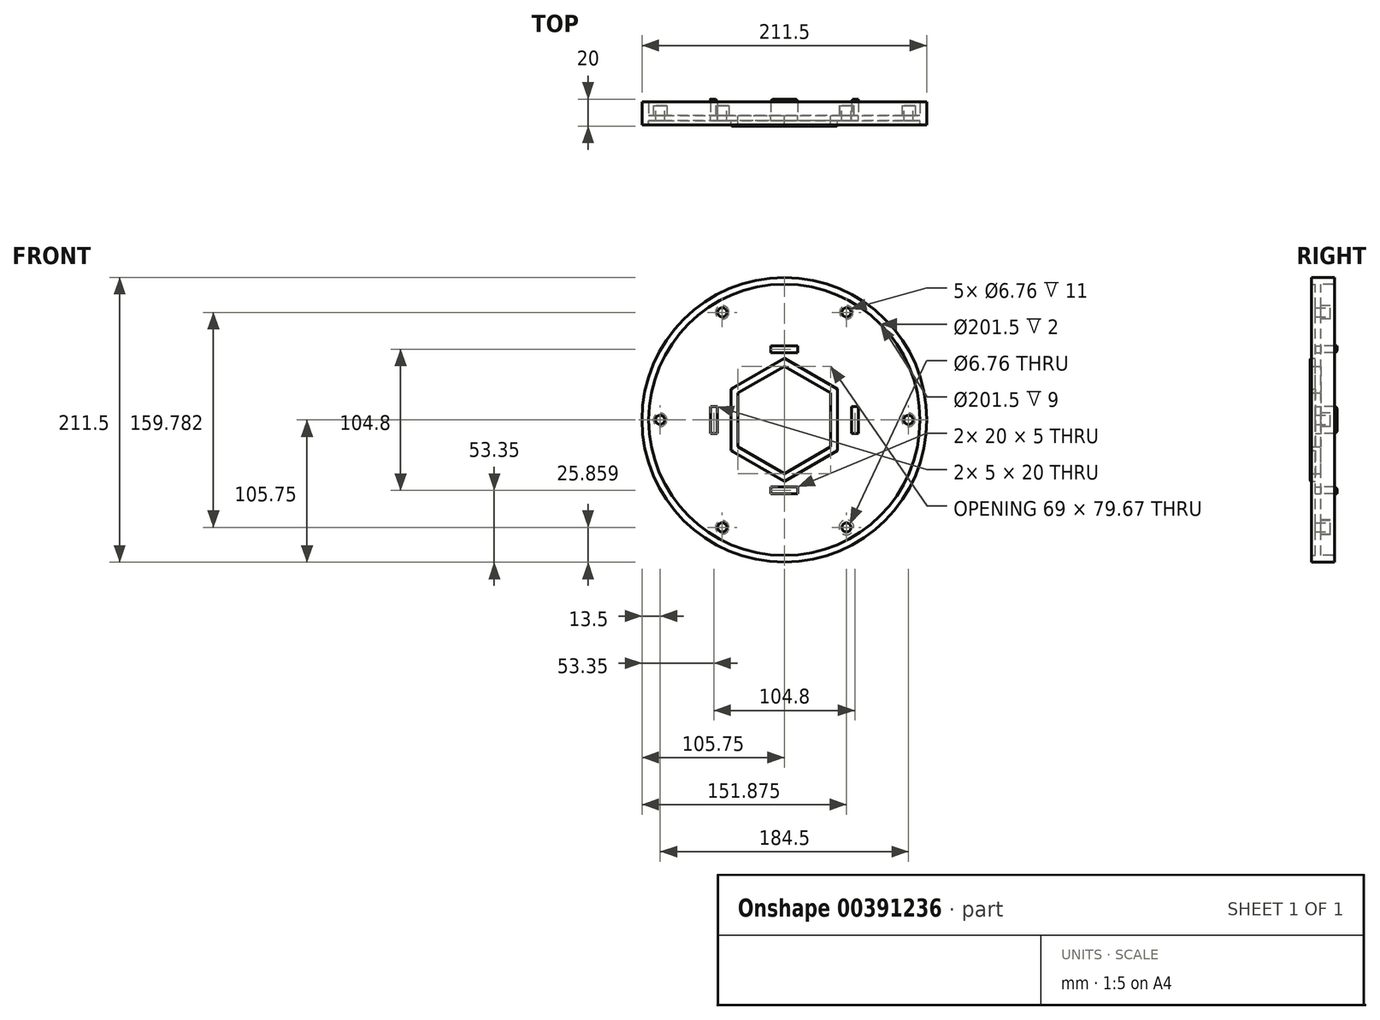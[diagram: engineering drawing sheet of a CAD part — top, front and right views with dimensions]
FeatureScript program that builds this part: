
annotation { "Feature Type Name" : "Feature", "Feature Type Description" : "" }
export const myFeature = defineFeature(function(context is Context, id is Id, definition is map)
    precondition{}
    {
        {
            var Q0;
            Q0=qCreatedBy(makeId("Front.planeOp"),FACE);
            var sketch = newSketch(context, id + "F0", { "sketchPlane" : qUnion([Q0])});
            skCircle(sketch, "E0.cCircle", {"center": v(0, 0) * mm, "radius": 80.5 * mm, "construction": true});
            skLineSegment(sketch, "E0.0", {"start": v(80.5, -46.48) * mm, "end": v(0, -92.95) * mm});
            skLineSegment(sketch, "E0.1", {"start": v(0, -92.95) * mm, "end": v(-80.5, -46.48) * mm});
            skLineSegment(sketch, "E0.2", {"start": v(-80.5, -46.48) * mm, "end": v(-80.5, 46.48) * mm});
            skLineSegment(sketch, "E0.3", {"start": v(-80.5, 46.48) * mm, "end": v(0, 92.95) * mm});
            skLineSegment(sketch, "E0.4", {"start": v(0, 92.95) * mm, "end": v(80.5, 46.48) * mm});
            skLineSegment(sketch, "E0.5", {"start": v(80.5, 46.48) * mm, "end": v(80.5, -46.48) * mm});
            skPoint(sketch, "E0.0.midPoint", {"position": v(40.25, -69.72) * mm});
            skPoint(sketch, "E1.0.midPoint", {"position": v(83.75, 0) * mm});
            skCircle(sketch, "E2", {"center": v(0, 0) * mm, "radius": 100.75 * mm});
            skPoint(sketch, "E3.0.midPoint", {"position": v(19.75, -35.93) * mm});
            skCircle(sketch, "E4.cCircle", {"center": v(0, 0) * mm, "radius": 34.5 * mm, "construction": true});
            skLineSegment(sketch, "E4.0", {"start": v(34.5, -19.92) * mm, "end": v(0, -39.84) * mm});
            skLineSegment(sketch, "E4.1", {"start": v(0, -39.84) * mm, "end": v(-34.5, -19.92) * mm});
            skLineSegment(sketch, "E4.2", {"start": v(-34.5, -19.92) * mm, "end": v(-34.5, 19.92) * mm});
            skLineSegment(sketch, "E4.3", {"start": v(-34.5, 19.92) * mm, "end": v(0, 39.84) * mm});
            skLineSegment(sketch, "E4.4", {"start": v(0, 39.84) * mm, "end": v(34.5, 19.92) * mm});
            skLineSegment(sketch, "E4.5", {"start": v(34.5, 19.92) * mm, "end": v(34.5, -19.92) * mm});
            skPoint(sketch, "E4.0.midPoint", {"position": v(17.25, -29.88) * mm});
            skPoint(sketch, "E5.visualSharp", {"position": v(0, 96.7) * mm});
            skPoint(sketch, "E6.visualSharp", {"position": v(83.75, 48.35) * mm});
            skPoint(sketch, "E7.visualSharp", {"position": v(83.75, -48.35) * mm});
            skPoint(sketch, "E8.visualSharp", {"position": v(0, -96.7) * mm});
            skPoint(sketch, "E9.visualSharp", {"position": v(-83.75, -48.35) * mm});
            skPoint(sketch, "E10.visualSharp", {"position": v(-83.75, 48.35) * mm});
            skPoint(sketch, "E11.visualSharp", {"position": v(39.66, 22.9) * mm});
            skPoint(sketch, "E12.visualSharp", {"position": v(39.58, -24.48) * mm});
            skPoint(sketch, "E13.visualSharp", {"position": v(-0.08, -47.38) * mm});
            skPoint(sketch, "E14.visualSharp", {"position": v(-39.66, -22.9) * mm});
            skPoint(sketch, "E15.visualSharp", {"position": v(-39.66, 22.9) * mm});
            skPoint(sketch, "E16.visualSharp", {"position": v(0, 45.8) * mm});
            skCircle(sketch, "E17.cCircle", {"center": v(0, 0) * mm, "radius": 77.5 * mm, "construction": true});
            skLineSegment(sketch, "E17.0", {"start": v(77.5, 44.74) * mm, "end": v(77.5, -44.74) * mm});
            skLineSegment(sketch, "E17.1", {"start": v(77.5, -44.74) * mm, "end": v(0, -89.49) * mm});
            skLineSegment(sketch, "E17.2", {"start": v(0, -89.49) * mm, "end": v(-77.5, -44.74) * mm});
            skLineSegment(sketch, "E17.3", {"start": v(-77.5, -44.74) * mm, "end": v(-77.5, 44.74) * mm});
            skLineSegment(sketch, "E17.4", {"start": v(-77.5, 44.74) * mm, "end": v(0, 89.49) * mm});
            skLineSegment(sketch, "E17.5", {"start": v(0, 89.49) * mm, "end": v(77.5, 44.74) * mm});
            skPoint(sketch, "E17.0.midPoint", {"position": v(77.5, 0) * mm});
            skCircle(sketch, "E18.cCircle", {"center": v(0, 0) * mm, "radius": 39.5 * mm, "construction": true});
            skLineSegment(sketch, "E18.0", {"start": v(39.5, -22.8) * mm, "end": v(0, -45.61) * mm});
            skLineSegment(sketch, "E18.1", {"start": v(0, -45.61) * mm, "end": v(-39.5, -22.8) * mm});
            skLineSegment(sketch, "E18.2", {"start": v(-39.5, -22.8) * mm, "end": v(-39.5, 22.8) * mm});
            skLineSegment(sketch, "E18.3", {"start": v(-39.5, 22.8) * mm, "end": v(0, 45.61) * mm});
            skLineSegment(sketch, "E18.4", {"start": v(0, 45.61) * mm, "end": v(39.5, 22.8) * mm});
            skLineSegment(sketch, "E18.5", {"start": v(39.5, 22.8) * mm, "end": v(39.5, -22.8) * mm});
            skPoint(sketch, "E18.0.midPoint", {"position": v(19.75, -34.2) * mm});
            skCircle(sketch, "E19", {"center": v(0, 0) * mm, "radius": 105.75 * mm});
            skPoint(sketch, "E20", {"position": v(-46.12, 79.9) * mm});
            skPoint(sketch, "E21", {"position": v(46.12, 79.9) * mm});
            skPoint(sketch, "E22", {"position": v(92.25, 0) * mm});
            skPoint(sketch, "E23", {"position": v(46.13, -79.9) * mm});
            skPoint(sketch, "E24", {"position": v(-46.12, -79.9) * mm});
            skPoint(sketch, "E25", {"position": v(-92.25, 0) * mm});
            skCircle(sketch, "E26.cCircle", {"center": v(0, 0) * mm, "radius": 49.9 * mm, "construction": true});
            skLineSegment(sketch, "E26.0", {"start": v(49.9, -49.9) * mm, "end": v(-49.9, -49.9) * mm});
            skLineSegment(sketch, "E26.1", {"start": v(-49.9, -49.9) * mm, "end": v(-49.9, 49.9) * mm});
            skLineSegment(sketch, "E26.2", {"start": v(-49.9, 49.9) * mm, "end": v(49.9, 49.9) * mm});
            skLineSegment(sketch, "E26.3", {"start": v(49.9, 49.9) * mm, "end": v(49.9, -49.9) * mm});
            skPoint(sketch, "E26.0.midPoint", {"position": v(0, -49.9) * mm});
            skCircle(sketch, "E27", {"center": v(46.12, 79.9) * mm, "radius": 5 * mm});
            skCircle(sketch, "E28", {"center": v(92.25, 0) * mm, "radius": 5 * mm});
            skCircle(sketch, "E29", {"center": v(46.13, -79.9) * mm, "radius": 5.54 * mm});
            skCircle(sketch, "E30", {"center": v(-46.12, -79.9) * mm, "radius": 5 * mm});
            skCircle(sketch, "E31", {"center": v(-92.25, 0) * mm, "radius": 5 * mm});
            skCircle(sketch, "E32", {"center": v(-46.12, 79.9) * mm, "radius": 5 * mm});
            skPoint(sketch, "E33", {"position": v(10, -49.9) * mm});
            skPoint(sketch, "E34", {"position": v(-10, -49.9) * mm});
            skPoint(sketch, "E35", {"position": v(-10, -54.9) * mm});
            skPoint(sketch, "E36", {"position": v(10, -54.9) * mm});
            skLineSegment(sketch, "E37", {"start": v(-10, -49.9) * mm, "end": v(-10, -54.9) * mm});
            skLineSegment(sketch, "E38", {"start": v(-10, -54.9) * mm, "end": v(10, -54.9) * mm});
            skLineSegment(sketch, "E39", {"start": v(10, -54.9) * mm, "end": v(10, -49.9) * mm});
            skPoint(sketch, "E40", {"position": v(49.9, 0) * mm});
            skPoint(sketch, "E41", {"position": v(0, 49.9) * mm});
            skPoint(sketch, "E42", {"position": v(-49.9, 0) * mm});
            skPoint(sketch, "E43", {"position": v(49.9, -10) * mm});
            skPoint(sketch, "E44", {"position": v(49.9, 10) * mm});
            skPoint(sketch, "E45", {"position": v(54.9, -10) * mm});
            skPoint(sketch, "E46", {"position": v(54.9, 10) * mm});
            skLineSegment(sketch, "E47", {"start": v(49.9, -10) * mm, "end": v(54.9, -10) * mm});
            skLineSegment(sketch, "E48", {"start": v(54.9, 10) * mm, "end": v(54.9, -10) * mm});
            skLineSegment(sketch, "E49", {"start": v(49.9, 10) * mm, "end": v(54.9, 10) * mm});
            skPoint(sketch, "E50", {"position": v(10, 49.9) * mm});
            skPoint(sketch, "E51", {"position": v(10, 54.9) * mm});
            skPoint(sketch, "E52", {"position": v(-10, 49.9) * mm});
            skPoint(sketch, "E53", {"position": v(-10, 54.9) * mm});
            skLineSegment(sketch, "E54", {"start": v(10, 49.9) * mm, "end": v(10, 54.9) * mm});
            skLineSegment(sketch, "E55", {"start": v(10, 54.9) * mm, "end": v(-10, 54.9) * mm});
            skLineSegment(sketch, "E56", {"start": v(-10, 54.9) * mm, "end": v(-10, 49.9) * mm});
            skPoint(sketch, "E57", {"position": v(-49.9, -10) * mm});
            skPoint(sketch, "E58", {"position": v(-54.9, -10) * mm});
            skPoint(sketch, "E59", {"position": v(-49.9, 10) * mm});
            skPoint(sketch, "E60", {"position": v(-54.9, 10) * mm});
            skLineSegment(sketch, "E61", {"start": v(-49.9, -10) * mm, "end": v(-54.9, -10) * mm});
            skLineSegment(sketch, "E62", {"start": v(-54.9, -10) * mm, "end": v(-54.9, 10) * mm});
            skLineSegment(sketch, "E63", {"start": v(-54.9, 10) * mm, "end": v(-49.9, 10) * mm});
            skSolve(sketch);
        }
        {
            var Q0;
            Q0=makeQuery(id+"F0.imprint","IMPRINT",FACE,{"disambiguationData":[TD([[makeQuery(id+"F0.imprint","IMPRINT",EDGE,{"derivedFrom":sQuery(id+"F0.wireOp",EDGE,"E0.0")}),1.0]])]});
            var Q1;
            Q1=makeQuery(id+"F0.imprint","IMPRINT",FACE,{"disambiguationData":[TD([[makeQuery(id+"F0.imprint","IMPRINT",EDGE,{"derivedFrom":sQuery(id+"F0.wireOp",EDGE,"E17.0")}),-1.0]])]});
            var Q2;
            {var subQ0=sQuery(id+"F0.wireOp",EDGE,"E26.1");var subQ1=sQuery(id+"F0.wireOp",EDGE,"E18.3");var subQ2=makeQuery(id+"F0.imprint","INTERSECT",VERTEX,{"derivedFrom":[subQ1,subQ0]});Q2=makeQuery(id+"F0.imprint","IMPRINT",FACE,{"disambiguationData":[TD([[makeQuery(id+"F0.imprint","IMPRINT",EDGE,{"disambiguationData":[TD([[subQ2,-1.0]])],"derivedFrom":subQ1}),1.0]])]});}
            var Q3;
            {var subQ0=sQuery(id+"F0.wireOp",EDGE,"E26.2");var subQ1=sQuery(id+"F0.wireOp",EDGE,"E18.4");var subQ2=makeQuery(id+"F0.imprint","INTERSECT",VERTEX,{"derivedFrom":[subQ1,subQ0]});Q3=makeQuery(id+"F0.imprint","IMPRINT",FACE,{"disambiguationData":[TD([[makeQuery(id+"F0.imprint","IMPRINT",EDGE,{"disambiguationData":[TD([[subQ2,-1.0]])],"derivedFrom":subQ1}),1.0]])]});}
            var Q4;
            {var subQ0=sQuery(id+"F0.wireOp",EDGE,"E26.0");var subQ1=sQuery(id+"F0.wireOp",EDGE,"E18.1");var subQ2=makeQuery(id+"F0.imprint","INTERSECT",VERTEX,{"derivedFrom":[subQ1,subQ0]});Q4=makeQuery(id+"F0.imprint","IMPRINT",FACE,{"disambiguationData":[TD([[makeQuery(id+"F0.imprint","IMPRINT",EDGE,{"disambiguationData":[TD([[subQ2,-1.0]])],"derivedFrom":subQ1}),1.0]])]});}
            var Q5;
            {var subQ0=sQuery(id+"F0.wireOp",EDGE,"E26.3");var subQ1=sQuery(id+"F0.wireOp",EDGE,"E18.0");var subQ2=makeQuery(id+"F0.imprint","INTERSECT",VERTEX,{"derivedFrom":[subQ1,subQ0]});Q5=makeQuery(id+"F0.imprint","IMPRINT",FACE,{"disambiguationData":[TD([[makeQuery(id+"F0.imprint","IMPRINT",EDGE,{"disambiguationData":[TD([[subQ2,-1.0]])],"derivedFrom":subQ1}),1.0]])]});}
            var Q6;
            {var subQ0=sQuery(id+"F0.wireOp",EDGE,"XCPQ21YX-vmVf-RJUl-SYTq-fUJmevbIAi7m");var subQ1=sQuery(id+"F0.wireOp",EDGE,"E18.0");var subQ2=makeQuery(id+"F0.imprint","INTERSECT",VERTEX,{"derivedFrom":[subQ1,subQ0]});Q6=makeQuery(id+"F0.imprint","IMPRINT",FACE,{"disambiguationData":[TD([[makeQuery(id+"F0.imprint","IMPRINT",EDGE,{"disambiguationData":[TD([[subQ2,-1.0]])],"derivedFrom":subQ1}),1.0]])]});}
            var Q7;
            Q7=makeQuery(id+"F0.imprint","IMPRINT",FACE,{"disambiguationData":[TD([[makeQuery(id+"F0.imprint","IMPRINT",EDGE,{"derivedFrom":sQuery(id+"F0.wireOp",EDGE,"E32")}),1.0]])]});
            var Q8;
            Q8=makeQuery(id+"F0.imprint","IMPRINT",FACE,{"disambiguationData":[TD([[makeQuery(id+"F0.imprint","IMPRINT",EDGE,{"derivedFrom":sQuery(id+"F0.wireOp",EDGE,"E27")}),1.0]])]});
            var Q9;
            Q9=makeQuery(id+"F0.imprint","IMPRINT",FACE,{"disambiguationData":[TD([[makeQuery(id+"F0.imprint","IMPRINT",EDGE,{"derivedFrom":sQuery(id+"F0.wireOp",EDGE,"E28")}),1.0]])]});
            var Q10;
            Q10=makeQuery(id+"F0.imprint","IMPRINT",FACE,{"disambiguationData":[TD([[makeQuery(id+"F0.imprint","IMPRINT",EDGE,{"derivedFrom":sQuery(id+"F0.wireOp",EDGE,"E29")}),1.0]])]});
            var Q11;
            Q11=makeQuery(id+"F0.imprint","IMPRINT",FACE,{"disambiguationData":[TD([[makeQuery(id+"F0.imprint","IMPRINT",EDGE,{"derivedFrom":sQuery(id+"F0.wireOp",EDGE,"E30")}),1.0]])]});
            var Q12;
            Q12=makeQuery(id+"F0.imprint","IMPRINT",FACE,{"disambiguationData":[TD([[makeQuery(id+"F0.imprint","IMPRINT",EDGE,{"derivedFrom":sQuery(id+"F0.wireOp",EDGE,"E31")}),1.0]])]});
            extrude(context, id + "F1", {"entities" : qUnion([Q0, Q1, Q2, Q3, Q4, Q5, Q6, Q7, Q8, Q9, Q10, Q11, Q12]), "depth" : 4 * mm});
        }
        {
            var Q0;
            Q0=makeQuery(id+"F0.imprint","IMPRINT",FACE,{"disambiguationData":[TD([[makeQuery(id+"F0.imprint","IMPRINT",EDGE,{"derivedFrom":sQuery(id+"F0.wireOp",EDGE,"E0.0")}),-1.0]])]});
            extrude(context, id + "F2", {"entities" : qUnion([Q0]), "depth" : 4 * mm});
        }
        {
            var Q0;
            Q0=makeQuery(id+"F0.imprint","IMPRINT",FACE,{"disambiguationData":[TD([[makeQuery(id+"F0.imprint","IMPRINT",EDGE,{"derivedFrom":sQuery(id+"F0.wireOp",EDGE,"E4.0")}),1.0]])]});
            var Q1;
            {var subQ5=sQuery(id+"F0.wireOp",EDGE,"E4.1");var subQ6=sQuery(id+"F0.wireOp",EDGE,"E4.0");var subQ7=makeQuery(id+"F0.imprint","INTERSECT",VERTEX,{"derivedFrom":[subQ6,subQ5]});Q1=makeQuery(id+"F0.imprint","IMPRINT",FACE,{"disambiguationData":[TD([[makeQuery(id+"F0.imprint","IMPRINT",EDGE,{"disambiguationData":[TD([[subQ7,1.0]])],"derivedFrom":subQ6}),1.0]])]});}
            var Q2;
            {var subQ0=sQuery(id+"F0.wireOp",EDGE,"E26.0");var subQ1=sQuery(id+"F0.wireOp",EDGE,"E4.1");var subQ2=makeQuery(id+"F0.imprint","INTERSECT",VERTEX,{"derivedFrom":[subQ1,subQ0]});Q2=makeQuery(id+"F0.imprint","IMPRINT",FACE,{"disambiguationData":[TD([[makeQuery(id+"F0.imprint","IMPRINT",EDGE,{"disambiguationData":[TD([[subQ2,-1.0]])],"derivedFrom":subQ1}),1.0]])]});}
            var Q3;
            {var subQ1=sQuery(id+"F0.wireOp",EDGE,"E4.2");Q3=makeQuery(id+"F0.imprint","IMPRINT",FACE,{"disambiguationData":[TD([[makeQuery(id+"F0.imprint","IMPRINT",EDGE,{"derivedFrom":subQ1}),1.0]])]});}
            var Q4;
            {var subQ0=sQuery(id+"F0.wireOp",EDGE,"E26.1");var subQ1=sQuery(id+"F0.wireOp",EDGE,"E4.3");var subQ2=makeQuery(id+"F0.imprint","INTERSECT",VERTEX,{"derivedFrom":[subQ1,subQ0]});Q4=makeQuery(id+"F0.imprint","IMPRINT",FACE,{"disambiguationData":[TD([[makeQuery(id+"F0.imprint","IMPRINT",EDGE,{"disambiguationData":[TD([[subQ2,-1.0]])],"derivedFrom":subQ1}),1.0]])]});}
            var Q5;
            {var subQ5=sQuery(id+"F0.wireOp",EDGE,"E4.4");var subQ6=sQuery(id+"F0.wireOp",EDGE,"E4.3");var subQ7=makeQuery(id+"F0.imprint","INTERSECT",VERTEX,{"derivedFrom":[subQ6,subQ5]});Q5=makeQuery(id+"F0.imprint","IMPRINT",FACE,{"disambiguationData":[TD([[makeQuery(id+"F0.imprint","IMPRINT",EDGE,{"disambiguationData":[TD([[subQ7,1.0]])],"derivedFrom":subQ6}),1.0]])]});}
            var Q6;
            {var subQ0=sQuery(id+"F0.wireOp",EDGE,"E26.2");var subQ1=sQuery(id+"F0.wireOp",EDGE,"E4.4");var subQ2=makeQuery(id+"F0.imprint","INTERSECT",VERTEX,{"derivedFrom":[subQ1,subQ0]});Q6=makeQuery(id+"F0.imprint","IMPRINT",FACE,{"disambiguationData":[TD([[makeQuery(id+"F0.imprint","IMPRINT",EDGE,{"disambiguationData":[TD([[subQ2,-1.0]])],"derivedFrom":subQ1}),1.0]])]});}
            var Q7;
            {var subQ0=sQuery(id+"F0.wireOp",EDGE,"E4.5");Q7=makeQuery(id+"F0.imprint","IMPRINT",FACE,{"disambiguationData":[TD([[makeQuery(id+"F0.imprint","IMPRINT",EDGE,{"derivedFrom":subQ0}),1.0]])]});}
            var Q8;
            {var subQ0=sQuery(id+"F0.wireOp",EDGE,"XCPQ21YX-vmVf-RJUl-SYTq-fUJmevbIAi7m");var subQ1=sQuery(id+"F0.wireOp",EDGE,"E4.0");var subQ2=makeQuery(id+"F0.imprint","INTERSECT",VERTEX,{"derivedFrom":[subQ1,subQ0]});Q8=makeQuery(id+"F0.imprint","IMPRINT",FACE,{"disambiguationData":[TD([[makeQuery(id+"F0.imprint","IMPRINT",EDGE,{"disambiguationData":[TD([[subQ2,-1.0]])],"derivedFrom":subQ1}),1.0]])]});}
            var Q9;
            {var subQ1=sQuery(id+"F0.wireOp",EDGE,"E4.0");var subQ5=sQuery(id+"F0.wireOp",EDGE,"nueKWM4Y-l1hd-9WO2-oQTT-vtyMg7v0kKZ8");var subQ9=makeQuery(id+"F0.imprint","INTERSECT",VERTEX,{"derivedFrom":[subQ1,subQ5]});Q9=makeQuery(id+"F0.imprint","IMPRINT",FACE,{"disambiguationData":[TD([[makeQuery(id+"F0.imprint","IMPRINT",EDGE,{"disambiguationData":[TD([[subQ9,-1.0]])],"derivedFrom":subQ1}),1.0]])]});}
            extrude(context, id + "F3", {"entities" : qUnion([Q0, Q1, Q2, Q3, Q4, Q5, Q6, Q7, Q8, Q9]), "operationType" : NewBodyOperationType.ADD, "depth" : 8 * mm});
        }
        {
            var Q0;
            Q0=makeQuery(id+"F0.imprint","IMPRINT",FACE,{"disambiguationData":[TD([[makeQuery(id+"F0.imprint","IMPRINT",EDGE,{"derivedFrom":sQuery(id+"F0.wireOp",EDGE,"E2")}),-1.0]])]});
            extrude(context, id + "F4", {"entities" : qUnion([Q0]), "operationType" : NewBodyOperationType.ADD, "depth" : 7 * mm});
        }
        {
            var Q0;
            Q0=makeQuery(id+"F1.opExtrude","SWEPT_BODY",BODY,{"disambiguationData":[OSD([sQuery(id+"F0.wireOp",EDGE,"E0.0"),sQuery(id+"F0.wireOp",EDGE,"E0.1"),sQuery(id+"F0.wireOp",EDGE,"E0.2"),sQuery(id+"F0.wireOp",EDGE,"E0.3"),sQuery(id+"F0.wireOp",EDGE,"E0.4"),sQuery(id+"F0.wireOp",EDGE,"E0.5"),sQuery(id+"F0.wireOp",EDGE,"E2")])]});
            var Q1;
            Q1=makeQuery(id+"F1.opExtrude","SWEPT_BODY",BODY,{"disambiguationData":[OSD([sQuery(id+"F0.wireOp",EDGE,"E17.0"),sQuery(id+"F0.wireOp",EDGE,"E17.1"),sQuery(id+"F0.wireOp",EDGE,"E17.2"),sQuery(id+"F0.wireOp",EDGE,"E17.3"),sQuery(id+"F0.wireOp",EDGE,"E17.4"),sQuery(id+"F0.wireOp",EDGE,"E17.5"),sQuery(id+"F0.wireOp",EDGE,"E18.0"),sQuery(id+"F0.wireOp",EDGE,"E18.1"),sQuery(id+"F0.wireOp",EDGE,"E18.2"),sQuery(id+"F0.wireOp",EDGE,"E18.3"),sQuery(id+"F0.wireOp",EDGE,"E18.4"),sQuery(id+"F0.wireOp",EDGE,"E18.5")])]});
            var Q2;
            Q2=makeQuery(id+"F2.opExtrude","SWEPT_BODY",BODY,{"disambiguationData":[OSD([sQuery(id+"F0.wireOp",EDGE,"E0.0"),sQuery(id+"F0.wireOp",EDGE,"E0.1"),sQuery(id+"F0.wireOp",EDGE,"E0.2"),sQuery(id+"F0.wireOp",EDGE,"E0.3"),sQuery(id+"F0.wireOp",EDGE,"E0.4"),sQuery(id+"F0.wireOp",EDGE,"E0.5"),sQuery(id+"F0.wireOp",EDGE,"E17.0"),sQuery(id+"F0.wireOp",EDGE,"E17.1"),sQuery(id+"F0.wireOp",EDGE,"E17.2"),sQuery(id+"F0.wireOp",EDGE,"E17.3"),sQuery(id+"F0.wireOp",EDGE,"E17.4"),sQuery(id+"F0.wireOp",EDGE,"E17.5")])]});
            booleanBodies(context, id + "F5", {"operationType" : BooleanOperationType.UNION, "tools" : qUnion([Q0, Q1, Q2])});
        }
        {
            var Q0;
            Q0=makeQuery(id+"F3.opExtrude","CAP_EDGE",EDGE,{"disambiguationData":[OSD([sQuery(id+"F0.wireOp",EDGE,"E18.4")])],"isStart":false});
            var Q1;
            Q1=makeQuery(id+"F3.opExtrude","CAP_EDGE",EDGE,{"disambiguationData":[OSD([sQuery(id+"F0.wireOp",EDGE,"E18.5")])],"isStart":false});
            var Q2;
            Q2=makeQuery(id+"F3.opExtrude","CAP_EDGE",EDGE,{"disambiguationData":[OSD([sQuery(id+"F0.wireOp",EDGE,"E18.0")])],"isStart":false});
            var Q3;
            Q3=makeQuery(id+"F3.opExtrude","CAP_EDGE",EDGE,{"disambiguationData":[OSD([sQuery(id+"F0.wireOp",EDGE,"E18.1")])],"isStart":false});
            var Q4;
            Q4=makeQuery(id+"F3.opExtrude","CAP_EDGE",EDGE,{"disambiguationData":[OSD([sQuery(id+"F0.wireOp",EDGE,"E18.2")])],"isStart":false});
            var Q5;
            Q5=makeQuery(id+"F3.opExtrude","CAP_EDGE",EDGE,{"disambiguationData":[OSD([sQuery(id+"F0.wireOp",EDGE,"E18.3")])],"isStart":false});
            fillet(context, id + "F6", {"entities" : qUnion([Q0, Q1, Q2, Q3, Q4, Q5]), "radius" : 1 * mm, "tangentPropagation" : true, "allowEdgeOverflow" : false});
        }
        {
            var Q0;
            Q0=sQuery(id+"F0.wireOp",VERTEX,"E20");
            var Q1;
            Q1=sQuery(id+"F0.wireOp",VERTEX,"E21");
            var Q2;
            Q2=sQuery(id+"F0.wireOp",VERTEX,"E22");
            var Q3;
            Q3=sQuery(id+"F0.wireOp",VERTEX,"E23");
            var Q4;
            Q4=sQuery(id+"F0.wireOp",VERTEX,"E24");
            var Q5;
            Q5=sQuery(id+"F0.wireOp",VERTEX,"E25");
            var Q6;
            Q6=makeQuery(id+"F1.opExtrude","SWEPT_BODY",BODY,{"disambiguationData":[OSD([sQuery(id+"F0.wireOp",EDGE,"E0.0"),sQuery(id+"F0.wireOp",EDGE,"E0.1"),sQuery(id+"F0.wireOp",EDGE,"E0.2"),sQuery(id+"F0.wireOp",EDGE,"E0.3"),sQuery(id+"F0.wireOp",EDGE,"E0.4"),sQuery(id+"F0.wireOp",EDGE,"E0.5"),sQuery(id+"F0.wireOp",EDGE,"E2")])]});
            hole(context, id + "F7", {"style" : HoleStyle.SIMPLE, "endStyle" : HoleEndStyle.THROUGH, "oppositeDirection" : true, "standardTappedOrClearance" : lookupTablePath({ "standard" : "ANSI", "fit" : "Normal (ASME)", "size" : "1/4", "type" : "Clearance" }), "standardBlindInLast" : lookupTablePath({ "fit" : "Free", "standard" : "ANSI", "size" : "1/4", "type" : "Clearance" }), "holeDiameter" : 6.76 * mm, "tappedDepth" : 12 * mm, "tapClearance" : 3, "locations" : qUnion([Q0, Q1, Q2, Q3, Q4, Q5]), "scope" : qUnion([Q6])});
        }
        {
            var Q0;
            Q0=makeQuery(id+"F4.opExtrude","CAP_EDGE",EDGE,{"disambiguationData":[OSD([sQuery(id+"F0.wireOp",EDGE,"E2")])],"isStart":false});
            fillet(context, id + "F8", {"entities" : qUnion([Q0]), "radius" : 1 * mm, "tangentPropagation" : true, "allowEdgeOverflow" : false});
        }
        {
            var Q0;
            Q0=makeQuery(id+"F0.imprint","IMPRINT",FACE,{"disambiguationData":[TD([[makeQuery(id+"F0.imprint","IMPRINT",EDGE,{"derivedFrom":sQuery(id+"F0.wireOp",EDGE,"E32")}),1.0]])]});
            var Q1;
            Q1=makeQuery(id+"F0.imprint","IMPRINT",FACE,{"disambiguationData":[TD([[makeQuery(id+"F0.imprint","IMPRINT",EDGE,{"derivedFrom":sQuery(id+"F0.wireOp",EDGE,"E27")}),1.0]])]});
            var Q2;
            Q2=makeQuery(id+"F0.imprint","IMPRINT",FACE,{"disambiguationData":[TD([[makeQuery(id+"F0.imprint","IMPRINT",EDGE,{"derivedFrom":sQuery(id+"F0.wireOp",EDGE,"E28")}),1.0]])]});
            var Q3;
            Q3=makeQuery(id+"F0.imprint","IMPRINT",FACE,{"disambiguationData":[TD([[makeQuery(id+"F0.imprint","IMPRINT",EDGE,{"derivedFrom":sQuery(id+"F0.wireOp",EDGE,"E29")}),1.0]])]});
            var Q4;
            Q4=makeQuery(id+"F0.imprint","IMPRINT",FACE,{"disambiguationData":[TD([[makeQuery(id+"F0.imprint","IMPRINT",EDGE,{"derivedFrom":sQuery(id+"F0.wireOp",EDGE,"E30")}),1.0]])]});
            var Q5;
            Q5=makeQuery(id+"F0.imprint","IMPRINT",FACE,{"disambiguationData":[TD([[makeQuery(id+"F0.imprint","IMPRINT",EDGE,{"derivedFrom":sQuery(id+"F0.wireOp",EDGE,"E31")}),1.0]])]});
            extrude(context, id + "F9", {"entities" : qUnion([Q0, Q1, Q2, Q3, Q4, Q5]), "operationType" : NewBodyOperationType.ADD, "oppositeDirection" : true, "depth" : 7 * mm});
        }
        {
            var Q0;
            Q0=makeQuery(id+"F0.imprint","IMPRINT",FACE,{"disambiguationData":[TD([[makeQuery(id+"F0.imprint","IMPRINT",EDGE,{"derivedFrom":sQuery(id+"F0.wireOp",EDGE,"E2")}),-1.0]])]});
            extrude(context, id + "F10", {"entities" : qUnion([Q0]), "operationType" : NewBodyOperationType.ADD, "oppositeDirection" : true, "depth" : 10 * mm});
        }
        {
            var Q0;
            Q0=sQuery(id+"F0.wireOp",VERTEX,"E32.center");
            var Q1;
            Q1=sQuery(id+"F0.wireOp",VERTEX,"E27.center");
            var Q2;
            Q2=sQuery(id+"F0.wireOp",VERTEX,"E22");
            var Q3;
            Q3=sQuery(id+"F0.wireOp",VERTEX,"E23");
            var Q4;
            Q4=sQuery(id+"F0.wireOp",VERTEX,"E24");
            var Q5;
            Q5=sQuery(id+"F0.wireOp",VERTEX,"E25");
            var Q6;
            Q6=makeQuery(id+"F1.opExtrude","SWEPT_BODY",BODY,{"disambiguationData":[OSD([sQuery(id+"F0.wireOp",EDGE,"E0.0"),sQuery(id+"F0.wireOp",EDGE,"E0.1"),sQuery(id+"F0.wireOp",EDGE,"E0.2"),sQuery(id+"F0.wireOp",EDGE,"E0.3"),sQuery(id+"F0.wireOp",EDGE,"E0.4"),sQuery(id+"F0.wireOp",EDGE,"E0.5"),sQuery(id+"F0.wireOp",EDGE,"E2")])]});
            hole(context, id + "F11", {"style" : HoleStyle.SIMPLE, "endStyle" : HoleEndStyle.THROUGH, "standardTappedOrClearance" : lookupTablePath({ "standard" : "ANSI", "fit" : "Normal (ASME)", "size" : "1/4", "type" : "Clearance" }), "standardBlindInLast" : lookupTablePath({ "fit" : "Free", "standard" : "ANSI", "size" : "1/4", "type" : "Clearance" }), "holeDiameter" : 6.76 * mm, "tappedDepth" : 12 * mm, "tapClearance" : 3, "locations" : qUnion([Q0, Q1, Q2, Q3, Q4, Q5]), "scope" : qUnion([Q6])});
        }
        {
            var Q0;
            Q0=makeQuery(id+"F10.opExtrude","CAP_EDGE",EDGE,{"disambiguationData":[OSD([sQuery(id+"F0.wireOp",EDGE,"E2")])],"isStart":false});
            fillet(context, id + "F12", {"entities" : qUnion([Q0]), "radius" : 1 * mm, "tangentPropagation" : true, "allowEdgeOverflow" : false});
        }
        {
            var Q0;
            {var subQ0=sQuery(id+"F0.wireOp",EDGE,"E37");Q0=makeQuery(id+"F0.imprint","IMPRINT",FACE,{"disambiguationData":[TD([[makeQuery(id+"F0.imprint","IMPRINT",EDGE,{"derivedFrom":subQ0}),1.0]])]});}
            var Q1;
            {var subQ0=sQuery(id+"F0.wireOp",EDGE,"E47");Q1=makeQuery(id+"F0.imprint","IMPRINT",FACE,{"disambiguationData":[TD([[makeQuery(id+"F0.imprint","IMPRINT",EDGE,{"derivedFrom":subQ0}),1.0]])]});}
            var Q2;
            {var subQ0=sQuery(id+"F0.wireOp",EDGE,"E54");Q2=makeQuery(id+"F0.imprint","IMPRINT",FACE,{"disambiguationData":[TD([[makeQuery(id+"F0.imprint","IMPRINT",EDGE,{"derivedFrom":subQ0}),1.0]])]});}
            var Q3;
            {var subQ0=sQuery(id+"F0.wireOp",EDGE,"E61");Q3=makeQuery(id+"F0.imprint","IMPRINT",FACE,{"disambiguationData":[TD([[makeQuery(id+"F0.imprint","IMPRINT",EDGE,{"derivedFrom":subQ0}),-1.0]])]});}
            extrude(context, id + "F13", {"entities" : qUnion([Q0, Q1, Q2, Q3]), "depth" : 4 * mm});
        }
        {
            var Q0;
            {var subQ0=sQuery(id+"F0.wireOp",EDGE,"E37");Q0=makeQuery(id+"F0.imprint","IMPRINT",FACE,{"disambiguationData":[TD([[makeQuery(id+"F0.imprint","IMPRINT",EDGE,{"derivedFrom":subQ0}),1.0]])]});}
            var Q1;
            {var subQ0=sQuery(id+"F0.wireOp",EDGE,"E47");Q1=makeQuery(id+"F0.imprint","IMPRINT",FACE,{"disambiguationData":[TD([[makeQuery(id+"F0.imprint","IMPRINT",EDGE,{"derivedFrom":subQ0}),1.0]])]});}
            var Q2;
            {var subQ0=sQuery(id+"F0.wireOp",EDGE,"E54");Q2=makeQuery(id+"F0.imprint","IMPRINT",FACE,{"disambiguationData":[TD([[makeQuery(id+"F0.imprint","IMPRINT",EDGE,{"derivedFrom":subQ0}),1.0]])]});}
            var Q3;
            {var subQ0=sQuery(id+"F0.wireOp",EDGE,"E61");Q3=makeQuery(id+"F0.imprint","IMPRINT",FACE,{"disambiguationData":[TD([[makeQuery(id+"F0.imprint","IMPRINT",EDGE,{"derivedFrom":subQ0}),-1.0]])]});}
            extrude(context, id + "F14", {"entities" : qUnion([Q0, Q1, Q2, Q3]), "oppositeDirection" : true, "depth" : 12 * mm});
        }
        {
            var Q0;
            Q0=makeQuery(id+"F14.opExtrude","CAP_EDGE",EDGE,{"disambiguationData":[OSD([sQuery(id+"F0.wireOp",EDGE,"E26.0")])],"isStart":false});
            var Q1;
            Q1=makeQuery(id+"F14.opExtrude","CAP_EDGE",EDGE,{"disambiguationData":[OSD([sQuery(id+"F0.wireOp",EDGE,"E26.3")])],"isStart":false});
            var Q2;
            Q2=makeQuery(id+"F14.opExtrude","CAP_EDGE",EDGE,{"disambiguationData":[OSD([sQuery(id+"F0.wireOp",EDGE,"E26.2")])],"isStart":false});
            var Q3;
            Q3=makeQuery(id+"F14.opExtrude","CAP_EDGE",EDGE,{"disambiguationData":[OSD([sQuery(id+"F0.wireOp",EDGE,"E26.1")])],"isStart":false});
            var Q4;
            Q4=makeQuery(id+"F14.opExtrude","SWEPT_EDGE",EDGE,{"disambiguationData":[OSD([sQuery(id+"F0.wireOp",EDGE,"E26.0"),sQuery(id+"F0.wireOp",EDGE,"E37")])]});
            var Q5;
            Q5=makeQuery(id+"F14.opExtrude","SWEPT_EDGE",EDGE,{"disambiguationData":[OSD([sQuery(id+"F0.wireOp",EDGE,"E26.3"),sQuery(id+"F0.wireOp",EDGE,"E49")])]});
            var Q6;
            Q6=makeQuery(id+"F14.opExtrude","SWEPT_EDGE",EDGE,{"disambiguationData":[OSD([sQuery(id+"F0.wireOp",EDGE,"E26.3"),sQuery(id+"F0.wireOp",EDGE,"E47")])]});
            var Q7;
            Q7=makeQuery(id+"F14.opExtrude","SWEPT_EDGE",EDGE,{"disambiguationData":[OSD([sQuery(id+"F0.wireOp",EDGE,"E26.0"),sQuery(id+"F0.wireOp",EDGE,"E39")])]});
            var Q8;
            Q8=makeQuery(id+"F14.opExtrude","SWEPT_EDGE",EDGE,{"disambiguationData":[OSD([sQuery(id+"F0.wireOp",EDGE,"E26.1"),sQuery(id+"F0.wireOp",EDGE,"E61")])]});
            var Q9;
            Q9=makeQuery(id+"F14.opExtrude","SWEPT_EDGE",EDGE,{"disambiguationData":[OSD([sQuery(id+"F0.wireOp",EDGE,"E26.1"),sQuery(id+"F0.wireOp",EDGE,"E63")])]});
            var Q10;
            Q10=makeQuery(id+"F14.opExtrude","SWEPT_EDGE",EDGE,{"disambiguationData":[OSD([sQuery(id+"F0.wireOp",EDGE,"E26.2"),sQuery(id+"F0.wireOp",EDGE,"E56")])]});
            var Q11;
            Q11=makeQuery(id+"F14.opExtrude","SWEPT_EDGE",EDGE,{"disambiguationData":[OSD([sQuery(id+"F0.wireOp",EDGE,"E26.2"),sQuery(id+"F0.wireOp",EDGE,"E54")])]});
            fillet(context, id + "F15", {"entities" : qUnion([Q0, Q1, Q2, Q3, Q4, Q5, Q6, Q7, Q8, Q9, Q10, Q11]), "radius" : 2 * mm, "tangentPropagation" : true, "allowEdgeOverflow" : false});
        }
        {
            var Q0;
            Q0=makeQuery(id+"F14.opExtrude","CAP_EDGE",EDGE,{"disambiguationData":[OSD([sQuery(id+"F0.wireOp",EDGE,"E37")])],"isStart":false});
            var Q1;
            Q1=makeQuery(id+"F14.opExtrude","CAP_EDGE",EDGE,{"disambiguationData":[OSD([sQuery(id+"F0.wireOp",EDGE,"E39")])],"isStart":false});
            var Q2;
            Q2=makeQuery(id+"F14.opExtrude","CAP_EDGE",EDGE,{"disambiguationData":[OSD([sQuery(id+"F0.wireOp",EDGE,"E49")])],"isStart":false});
            var Q3;
            Q3=makeQuery(id+"F14.opExtrude","CAP_EDGE",EDGE,{"disambiguationData":[OSD([sQuery(id+"F0.wireOp",EDGE,"E47")])],"isStart":false});
            var Q4;
            Q4=makeQuery(id+"F14.opExtrude","CAP_EDGE",EDGE,{"disambiguationData":[OSD([sQuery(id+"F0.wireOp",EDGE,"E54")])],"isStart":false});
            var Q5;
            Q5=makeQuery(id+"F14.opExtrude","CAP_EDGE",EDGE,{"disambiguationData":[OSD([sQuery(id+"F0.wireOp",EDGE,"E56")])],"isStart":false});
            var Q6;
            Q6=makeQuery(id+"F14.opExtrude","CAP_EDGE",EDGE,{"disambiguationData":[OSD([sQuery(id+"F0.wireOp",EDGE,"E63")])],"isStart":false});
            var Q7;
            Q7=makeQuery(id+"F14.opExtrude","CAP_EDGE",EDGE,{"disambiguationData":[OSD([sQuery(id+"F0.wireOp",EDGE,"E61")])],"isStart":false});
            fillet(context, id + "F16", {"entities" : qUnion([Q0, Q1, Q2, Q3, Q4, Q5, Q6, Q7]), "radius" : 2 * mm, "tangentPropagation" : true, "allowEdgeOverflow" : false});
        }
    });
